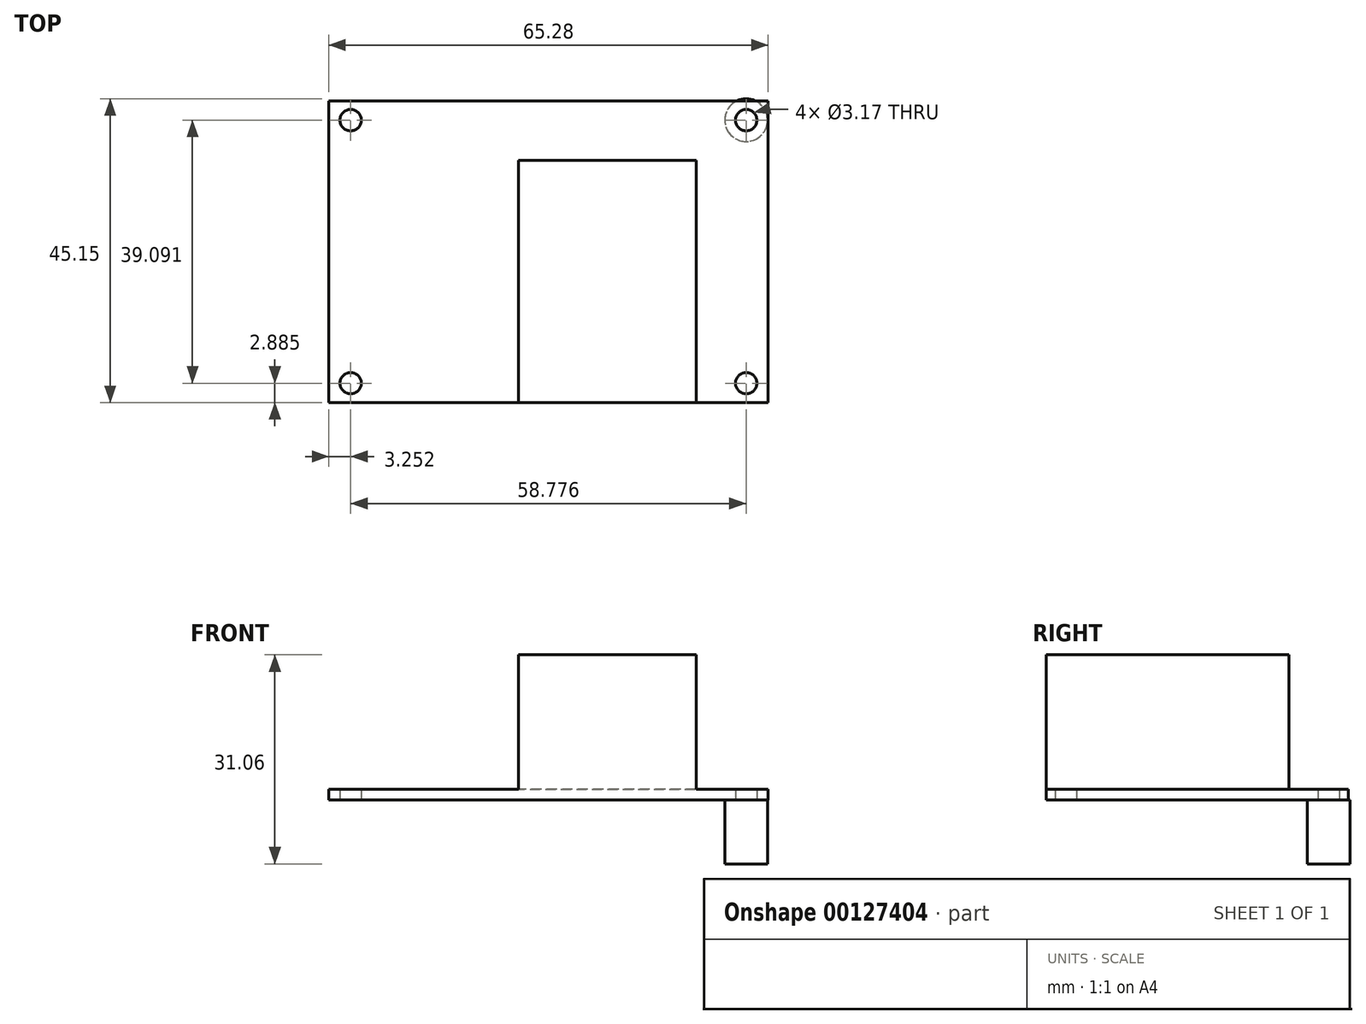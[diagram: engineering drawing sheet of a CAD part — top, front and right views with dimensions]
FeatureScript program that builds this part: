
annotation { "Feature Type Name" : "Feature", "Feature Type Description" : "" }
export const myFeature = defineFeature(function(context is Context, id is Id, definition is map)
    precondition{}
    {
        {
            var Q0;
            Q0=qCreatedBy(makeId("Top.planeOp"),FACE);
            var sketch = newSketch(context, id + "F0", { "sketchPlane" : qUnion([Q0])});
            skLineSegment(sketch, "E0.bottom", {"start": v(-32.64, -22.43) * mm, "end": v(32.64, -22.43) * mm});
            skLineSegment(sketch, "E0.top", {"start": v(-32.64, 22.43) * mm, "end": v(32.64, 22.43) * mm});
            skLineSegment(sketch, "E0.left", {"start": v(-32.64, -22.43) * mm, "end": v(-32.64, 22.43) * mm});
            skLineSegment(sketch, "E0.right", {"start": v(32.64, -22.43) * mm, "end": v(32.64, 22.43) * mm});
            skPoint(sketch, "E0.middle", {"position": v(0, 0) * mm});
            skCircle(sketch, "E1", {"center": v(-29.39, -19.55) * mm, "radius": 1.59 * mm});
            skCircle(sketch, "E2.MirrorC", {"center": v(29.39, -19.55) * mm, "radius": 1.59 * mm});
            skCircle(sketch, "E3.MirrorC", {"center": v(-29.39, 19.55) * mm, "radius": 1.59 * mm});
            skCircle(sketch, "E4.MirrorC", {"center": v(29.39, 19.55) * mm, "radius": 1.59 * mm});
            skSolve(sketch);
        }
        {
            var Q0;
            Q0 = qSketchRegion(id + "F0", true);
            extrude(context, id + "F1", {"entities" : qUnion([Q0]), "depth" : 1.57 * mm});
        }
        {
            var Q0;
            Q0=qCreatedBy(makeId("Top.planeOp"),FACE);
            var sketch = newSketch(context, id + "F2", { "sketchPlane" : qUnion([Q0])});
            skLineSegment(sketch, "E5.bottom", {"start": v(-4.44, 13.59) * mm, "end": v(21.97, 13.59) * mm});
            skLineSegment(sketch, "E5.top", {"start": v(-4.44, -22.43) * mm, "end": v(21.97, -22.43) * mm});
            skLineSegment(sketch, "E5.left", {"start": v(-4.44, 13.59) * mm, "end": v(-4.44, -22.43) * mm});
            skLineSegment(sketch, "E5.right", {"start": v(21.97, 13.59) * mm, "end": v(21.97, -22.43) * mm});
            skPoint(sketch, "E5.middle", {"position": v(8.76, -4.42) * mm});
            skSolve(sketch);
        }
        {
            var Q0;
            Q0 = qSketchRegion(id + "F2", true);
            extrude(context, id + "F3", {"entities" : qUnion([Q0]), "operationType" : NewBodyOperationType.ADD, "depth" : 21.53 * mm});
        }
        {
            var Q0;
            Q0=qCreatedBy(makeId("Top.planeOp"),FACE);
            var sketch = newSketch(context, id + "F4", { "sketchPlane" : qUnion([Q0])});
            skCircle(sketch, "E6", {"center": v(29.39, 19.55) * mm, "radius": 3.18 * mm});
            skSolve(sketch);
        }
        {
            var Q0;
            Q0 = qSketchRegion(id + "F4", true);
            extrude(context, id + "F5", {"entities" : qUnion([Q0]), "oppositeDirection" : true, "depth" : 9.52 * mm});
        }
    });
